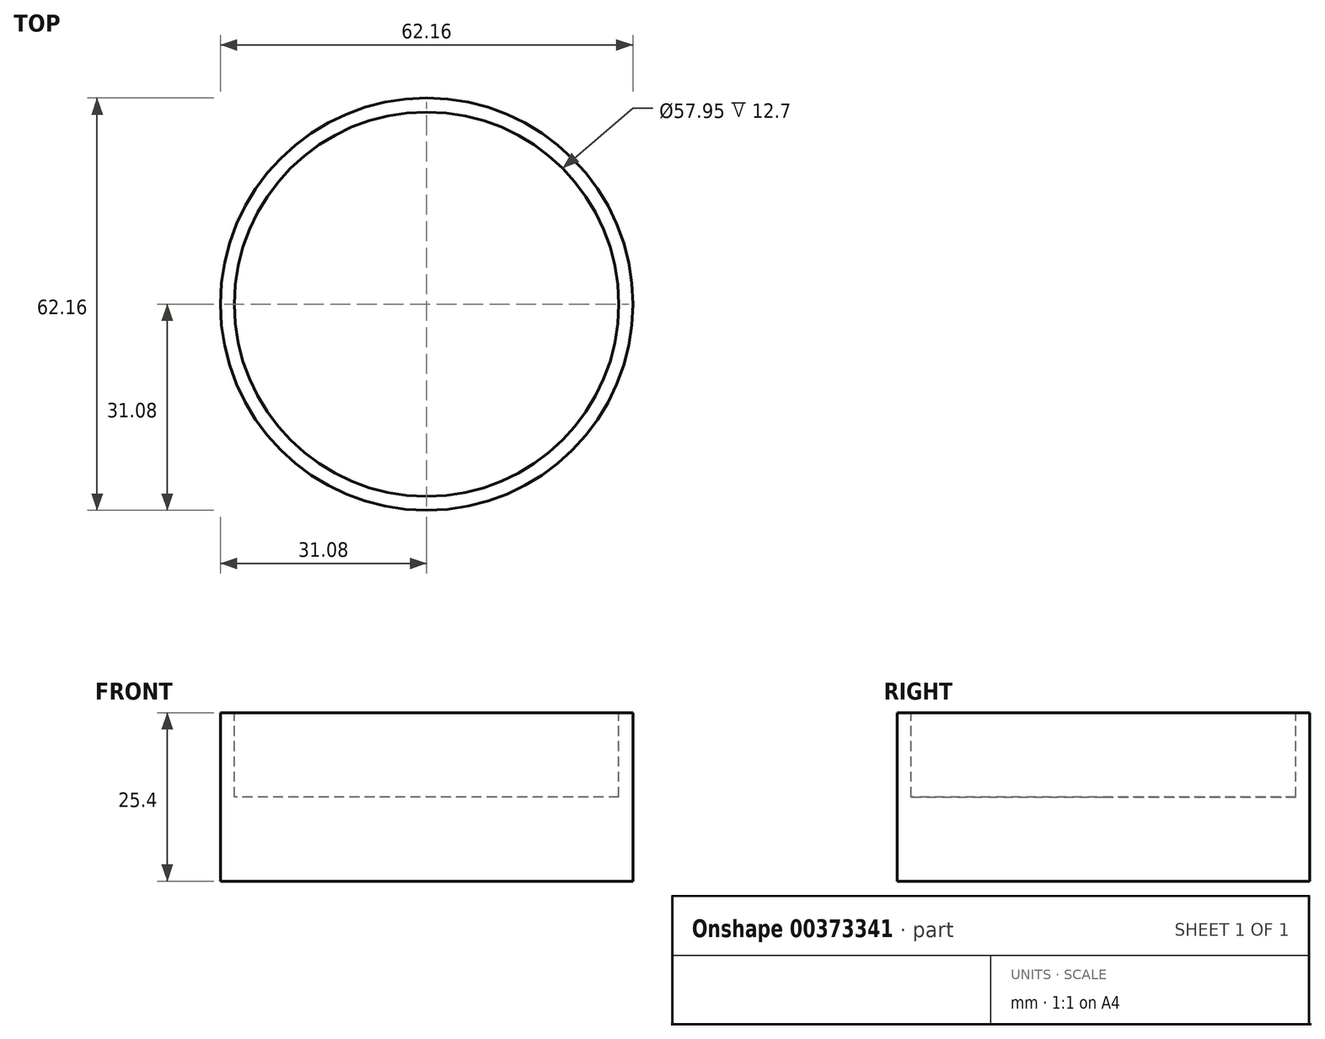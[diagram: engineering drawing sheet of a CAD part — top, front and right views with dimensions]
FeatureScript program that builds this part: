
annotation { "Feature Type Name" : "Feature", "Feature Type Description" : "" }
export const myFeature = defineFeature(function(context is Context, id is Id, definition is map)
    precondition{}
    {
        {
            var Q0;
            Q0=qCreatedBy(makeId("Top.planeOp"),FACE);
            var sketch = newSketch(context, id + "F0", { "sketchPlane" : qUnion([Q0])});
            skLineSegment(sketch, "E0", {"start": v(0, 63.5) * mm, "end": v(0, 0) * mm});
            skLineSegment(sketch, "E1", {"start": v(0, 0) * mm, "end": v(63.5, 0) * mm});
            skLineSegment(sketch, "E2", {"start": v(63.5, 0) * mm, "end": v(63.5, 63.5) * mm});
            skLineSegment(sketch, "E3", {"start": v(63.5, 63.5) * mm, "end": v(0, 63.5) * mm});
            skSolve(sketch);
        }
        {
            var Q0;
            Q0=makeQuery(id+"F0.imprint","IMPRINT",FACE,{"disambiguationData":[TD([[makeQuery(id+"F0.imprint","IMPRINT",EDGE,{"derivedFrom":sQuery(id+"F0.wireOp",EDGE,"E0")}),1.0]])]});
            extrude(context, id + "F1", {"entities" : qUnion([Q0]), "depth" : 25.4 * mm});
        }
        {
            var Q0;
            Q0=makeQuery(id+"F1.opExtrude","CAP_FACE",FACE,{"disambiguationData":[OSD([sQuery(id+"F0.wireOp",EDGE,"E0"),sQuery(id+"F0.wireOp",EDGE,"E1"),sQuery(id+"F0.wireOp",EDGE,"E2"),sQuery(id+"F0.wireOp",EDGE,"E3")])],"isStart":false});
            var sketch = newSketch(context, id + "F2", { "sketchPlane" : qUnion([Q0])});
            skLineSegment(sketch, "E4", {"start": v(31.75, 63.5) * mm, "end": v(31.75, 0) * mm});
            skLineSegment(sketch, "E5", {"start": v(0, 31.75) * mm, "end": v(63.5, 31.75) * mm});
            skCircle(sketch, "E6", {"center": v(31.75, 31.75) * mm, "radius": 31.08 * mm});
            skSolve(sketch);
        }
        {
            var Q0;
            {var subQ0=makeQuery(id+"F1.opExtrude","CAP_EDGE",EDGE,{"disambiguationData":[OSD([sQuery(id+"F0.wireOp",EDGE,"E3")])],"isStart":false});var subQ6=sQuery(id+"F2.wireOp",EDGE,"E4");var subQ9=makeQuery(id+"F2.imprint","INTERSECT",VERTEX,{"derivedFrom":[subQ0,subQ6]});Q0=makeQuery(id+"F2.imprint","IMPRINT",FACE,{"disambiguationData":[TD([[makeQuery(id+"F2.imprint","IMPRINT",EDGE,{"disambiguationData":[TD([[subQ9,-1.0]])],"derivedFrom":subQ6}),-1.0]])]});}
            var Q1;
            {var subQ1=sQuery(id+"F2.wireOp",EDGE,"E4");var subQ5=makeQuery(id+"F1.opExtrude","CAP_EDGE",EDGE,{"disambiguationData":[OSD([sQuery(id+"F0.wireOp",EDGE,"E3")])],"isStart":false});var subQ8=makeQuery(id+"F2.imprint","INTERSECT",VERTEX,{"derivedFrom":[subQ5,subQ1]});Q1=makeQuery(id+"F2.imprint","IMPRINT",FACE,{"disambiguationData":[TD([[makeQuery(id+"F2.imprint","IMPRINT",EDGE,{"disambiguationData":[TD([[subQ8,-1.0]])],"derivedFrom":subQ1}),1.0]])]});}
            var Q2;
            {var subQ1=makeQuery(id+"F1.opExtrude","CAP_EDGE",EDGE,{"disambiguationData":[OSD([sQuery(id+"F0.wireOp",EDGE,"E1")])],"isStart":false});var subQ3=sQuery(id+"F2.wireOp",EDGE,"E4");var subQ4=makeQuery(id+"F2.imprint","INTERSECT",VERTEX,{"derivedFrom":[subQ1,subQ3]});Q2=makeQuery(id+"F2.imprint","IMPRINT",FACE,{"disambiguationData":[TD([[makeQuery(id+"F2.imprint","IMPRINT",EDGE,{"disambiguationData":[TD([[subQ4,1.0]])],"derivedFrom":subQ3}),1.0]])]});}
            var Q3;
            {var subQ1=sQuery(id+"F2.wireOp",EDGE,"E4");var subQ7=makeQuery(id+"F1.opExtrude","CAP_EDGE",EDGE,{"disambiguationData":[OSD([sQuery(id+"F0.wireOp",EDGE,"E1")])],"isStart":false});var subQ9=makeQuery(id+"F2.imprint","INTERSECT",VERTEX,{"derivedFrom":[subQ7,subQ1]});Q3=makeQuery(id+"F2.imprint","IMPRINT",FACE,{"disambiguationData":[TD([[makeQuery(id+"F2.imprint","IMPRINT",EDGE,{"disambiguationData":[TD([[subQ9,1.0]])],"derivedFrom":subQ1}),-1.0]])]});}
            extrude(context, id + "F3", {"entities" : qUnion([Q0, Q1, Q2, Q3]), "operationType" : NewBodyOperationType.REMOVE, "oppositeDirection" : true, "depth" : 25.4 * mm});
        }
        {
            var Q0;
            Q0=makeQuery(id+"F1.opExtrude","CAP_FACE",FACE,{"disambiguationData":[OSD([sQuery(id+"F0.wireOp",EDGE,"E0"),sQuery(id+"F0.wireOp",EDGE,"E1"),sQuery(id+"F0.wireOp",EDGE,"E2"),sQuery(id+"F0.wireOp",EDGE,"E3")])],"isStart":false});
            var sketch = newSketch(context, id + "F4", { "sketchPlane" : qUnion([Q0])});
            skCircle(sketch, "E7", {"center": v(31.75, 31.75) * mm, "radius": 28.97 * mm});
            skSolve(sketch);
        }
        {
            var Q0;
            Q0 = qSketchRegion(id + "F4", true);
            extrude(context, id + "F5", {"entities" : qUnion([Q0]), "operationType" : NewBodyOperationType.REMOVE, "oppositeDirection" : true, "depth" : 12.7 * mm});
        }
    });
